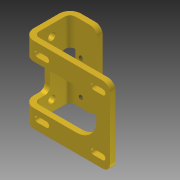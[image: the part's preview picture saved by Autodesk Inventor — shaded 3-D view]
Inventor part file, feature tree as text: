
AUTODESK INVENTOR PART (.ipt)
format: ipt  version: 2015 (Build 190159000, 159)  size: 319,488 bytes
history: native  units: mm
features: extrude x7, fillet x6, hole x2, other x1
ambient origin geometry x8: Origin, YZ Plane, XZ Plane, XY Plane, X Axis, Y Axis, Z Axis, Center Point
bodies: Solid1 (feature_tree)
feature tree (16):
  extrude  "Extrusión1"  Depth=3.0mm
  fillet  "Empalme1"  Radius=3.0mm
  extrude  "Extrusión2"  Depth=26.0mm
  extrude  "Extrusión3"  Depth=18.0mm
  hole  "Agujero1"  [1 undecoded]
  hole  "Agujero2"  [1 undecoded]
  fillet  "Empalme2"  Radius=3.0mm
  extrude  "Extrusión5"  Depth=6.0mm
  fillet  "Empalme3"  Radius=22.15mm
  extrude  "Extrusión9"  Depth=12.0mm TaperAngle=0.0deg
  fillet  "Redondeo de esquina3"  Radius=18.5mm
  extrude  "Extrusión10"  Depth=31.0mm
  extrude  "Extrusión8"  Depth=8.0mm
  fillet  "Redondeo de esquina1"  Radius=5.0mm
  fillet  "Redondeo de esquina2"  Radius=30.0mm
  other  "Definición1"
note: 2 required parameter values undecoded (feature->parameter linkage not recoverable at this tier; creation-order binding heuristic only, values carry confidence <= 0.55)
